# Revit family: IS_UltraFlatS_K8256_BIM_DE
name_source: partatom
category: Plumbing Fixtures
revit_build: Autodesk Revit MEP 2016 (Build: 20161004_0715(x64)
units: mm (PartAtom-declared; Revit-internal decimal feet)

## family parameters
Cut with Voids When Loaded = No
Host = Face
OmniClass Number = 23.45.05.14.21.11
OmniClass Title = Bath/Shower Units
Part Type = Normal
Room Calculation Point = No
Round Connector Dimension = Use Diameter
Shared = No

## types (5) — shared parameters
Accessories = www.idealstandard.de\ersatzteile
AreaUnits = millimeters
Assembly Code = C1030200
AssetType = Fixed
Brand = Ideal Standard
CodePerformance = 0
ConnectionType = Plumbing
CurrencyUnit = €
DurationUnit = year
ExpectedLife = 25
Features = ULTRA FLAT S rectangular shower tray 1400x900mm
GrossWeight = 45,5 kg
InstallationDate = 1900-12-31T23:59:59
InstallationInstructions = www.idealstandard.de\produkte
LinearUnits = millimeters
ManufacturerURL = www.idealstandard.de
Material = Sanitary Brass
NominalHeight = 30 mm  [stored 0.0984252 ft]
NominalLength = 1400 mm
NominalWidth = 900 mm
ProductInformation = www.idealstandard.de
Shape = Rectangular
Size = 900 x 1400 x 30 mm
Space = Internal
URL = www.idealstandard.de
Uniclass2015Code = Pr_40_20_06_84
Uniclass2015Title = Shower trays
Uniclass2015Version = Products v1.1
Version = 1
VolumeUnits = Litres
zero-valued in all types: CWFU, Cost, Default Elevation, HWFU, NominalDepth, WFU

## per-type parameters (varying)
| type | BIMObjectName | BarCode | Color | Description | Finish | MainMaterial | Model | ModelNumber | ModelReference | Name |
| K8256FR - ULTRAFLAT S PD 140X90 BIANCO | ISI_IdealStandard_Showers_Ultra Flat S_K8256FR | 4015413067720 | Pure White | Ultraflat S Pd 140 x 90 Bianco | Pure White | IS_RenderMaterial_White | K8256FR | K8256FR | IS Rechteck-Brausewanne ULTRA FLAT S, 1400x900x30mm, Carraraweiß | ISI_IdealStandard_Showers_Ultra Flat S_K8256FR |
| K8256FS - ULTRAFLAT S PD 140X90 GRIGIO CEMENTO | ISI_IdealStandard_Showers_Ultra Flat S_K8256FS | 4015413070706 | Concrete Grey | Ultraflat S Pd 140 x 90 Grigio Cemento | Concrete Grey | IS_RenderMaterial_Grey | K8256FS | K8256FS | IS Rechteck-Brausewanne ULTRA FLAT S, 1400x900x30mm, Quarzgrau | ISI_IdealStandard_Showers_Ultra Flat S_K8256FS |
| K8256FT - ULTRAFLAT S PD 140X90 SABBIA | ISI_IdealStandard_Showers_Ultra Flat S_K8256FT | 4015413071093 | Beach Sand | Ultraflat S Pd 140 x 90 Sabbia | Beach Sand | IS_RenderMaterial_Sand | K8256FT | K8256FT | IS Rechteck-Brausewanne ULTRA FLAT S, 1400x900x30mm, Sandstein | ISI_IdealStandard_Showers_Ultra Flat S_K8256FT |
| K8256FV - ULTRAFLAT S PD 140X90 NERO | ISI_IdealStandard_Showers_Ultra Flat S_K8256FV | 4015413071826 | Jet Black | Ultraflat S Pd 140 x 90 Nero | Jet Black | IS_RenderMaterial_Black | K8256FV | K8256FV | IS Rechteck-Brausewanne ULTRA FLAT S, 1400x900x30mm, Schiefer | ISI_IdealStandard_Showers_Ultra Flat S_K8256FV |
| K8256FU - ULTRAFLAT S PD 140X90 MOKA | ISI_IdealStandard_Showers_Ultra Flat S_K8256FU | 4015413071505 | Deep Moka | Ultraflat S Pd 140 x 90 Moka | Deep Moka | IS_RenderMaterial_Moka | K8256FU | K8256FU | IS Rechteck-Brausewanne ULTRA FLAT S, 1400x900x30mm, Lavabraun | ISI_IdealStandard_Showers_Ultra Flat S_K8256FU |

note: [stored X ft] marks values corroborated as IEEE doubles in the binary element streams (Revit-internal decimal feet)

## geometry (parser evidence)
native form markers: Blend x4, Sweep x2
no freeform markers — native parametric forms only
